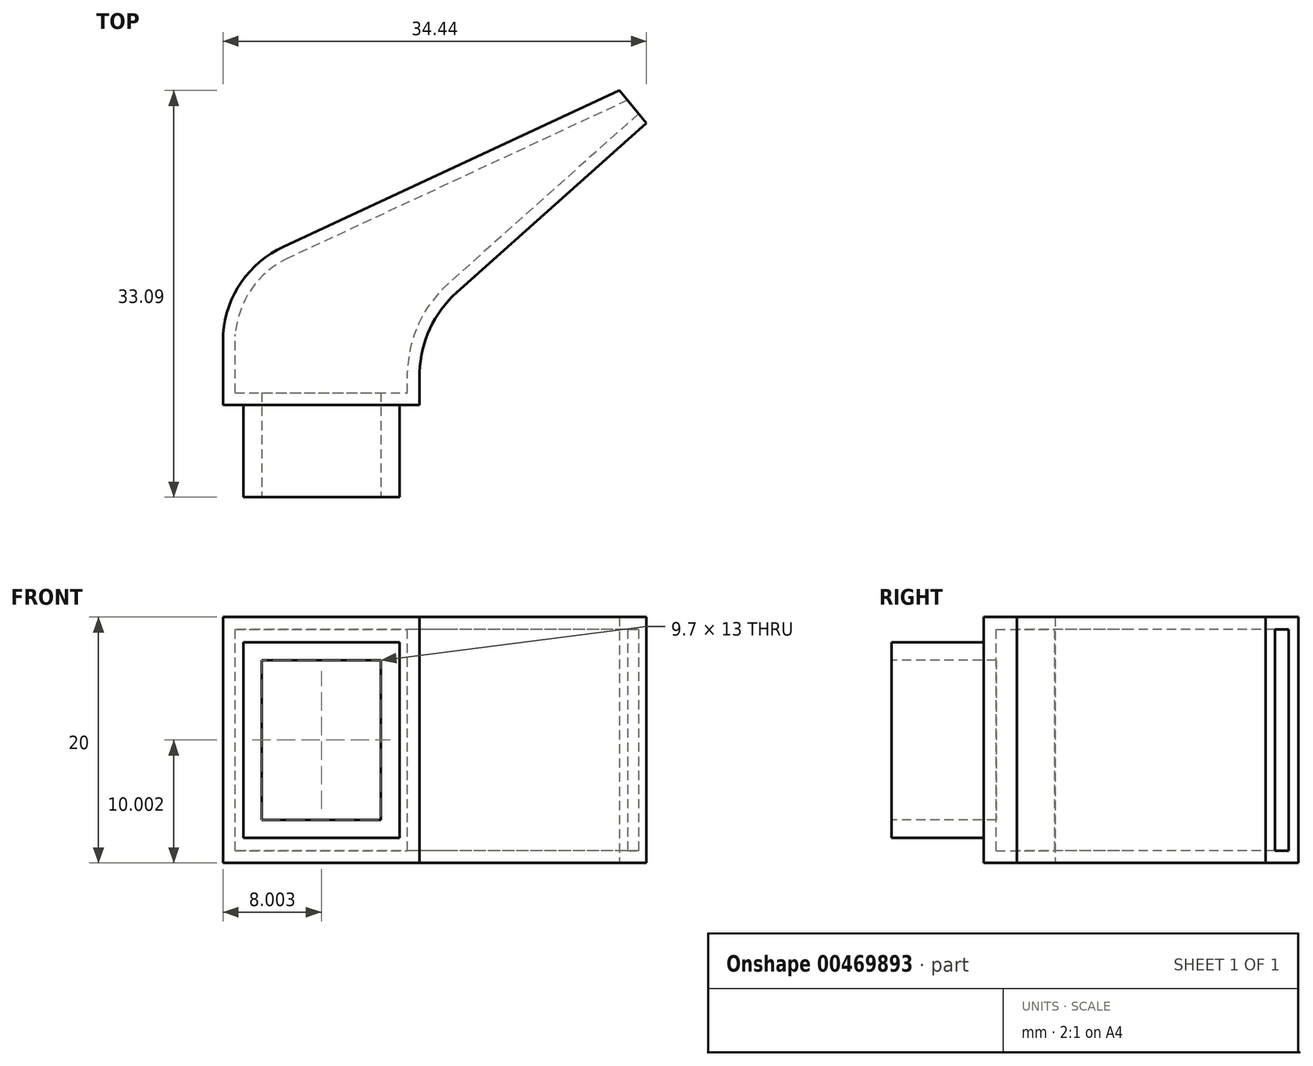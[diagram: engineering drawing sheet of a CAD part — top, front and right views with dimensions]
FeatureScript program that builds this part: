
annotation { "Feature Type Name" : "Feature", "Feature Type Description" : "" }
export const myFeature = defineFeature(function(context is Context, id is Id, definition is map)
    precondition{}
    {
        {
            var Q0;
            Q0=qCreatedBy(makeId("Front.planeOp"),FACE);
            var sketch = newSketch(context, id + "F0", { "sketchPlane" : qUnion([Q0])});
            skLineSegment(sketch, "E0.bottom", {"start": v(-17.22, 10) * mm, "end": v(17.22, 10) * mm});
            skLineSegment(sketch, "E0.top", {"start": v(-17.22, -10) * mm, "end": v(17.22, -10) * mm});
            skLineSegment(sketch, "E0.left", {"start": v(-17.22, 10) * mm, "end": v(-17.22, -10) * mm});
            skPoint(sketch, "E0.middle", {"position": v(0.21, 0.04) * mm});
            skPoint(sketch, "E1.middle", {"position": v(-0.07, 0.04) * mm});
            skLineSegment(sketch, "E2.bottom", {"start": v(-14.07, 6.5) * mm, "end": v(-4.37, 6.5) * mm});
            skLineSegment(sketch, "E2.top", {"start": v(-14.07, -6.5) * mm, "end": v(-4.37, -6.5) * mm});
            skLineSegment(sketch, "E2.left", {"start": v(-14.07, 6.5) * mm, "end": v(-14.07, -6.5) * mm});
            skLineSegment(sketch, "E2.right", {"start": v(-4.37, 6.5) * mm, "end": v(-4.37, -6.5) * mm});
            skLineSegment(sketch, "E3.bottom", {"start": v(-15.57, 7.96) * mm, "end": v(-2.87, 7.96) * mm});
            skLineSegment(sketch, "E3.top", {"start": v(-15.57, -7.96) * mm, "end": v(-2.87, -7.96) * mm});
            skLineSegment(sketch, "E3.left", {"start": v(-15.57, 7.96) * mm, "end": v(-15.57, -7.96) * mm});
            skLineSegment(sketch, "E3.right", {"start": v(-2.87, 7.96) * mm, "end": v(-2.87, -7.96) * mm});
            skLineSegment(sketch, "E4.0", {"start": v(17.22, 10) * mm, "end": v(17.22, -10) * mm});
            skLineSegment(sketch, "E5.0", {"start": v(-1.22, 10) * mm, "end": v(-1.22, -10) * mm});
            skSolve(sketch);
        }
        {
            var Q0;
            Q0=qCreatedBy(makeId("Top.planeOp"),FACE);
            var sketch = newSketch(context, id + "F1", { "sketchPlane" : qUnion([Q0])});
            skLineSegment(sketch, "E6.bottom", {"start": v(-15.57, -7.3) * mm, "end": v(-2.87, -7.3) * mm});
            skLineSegment(sketch, "E6.top", {"start": v(-15.57, 0) * mm, "end": v(-2.87, 0) * mm});
            skLineSegment(sketch, "E6.left", {"start": v(-15.57, -7.3) * mm, "end": v(-15.57, 0) * mm});
            skLineSegment(sketch, "E6.right", {"start": v(-2.87, -7.3) * mm, "end": v(-2.87, 0) * mm});
            skLineSegment(sketch, "E7", {"start": v(-15.57, 0) * mm, "end": v(-17.22, 0) * mm});
            skLineSegment(sketch, "E8", {"start": v(-2.87, 0) * mm, "end": v(-1.22, 0) * mm});
            skLineSegment(sketch, "E9", {"start": v(15.02, 25.59) * mm, "end": v(17.22, 22.91) * mm});
            skLineSegment(sketch, "E10", {"start": v(15.02, 25.59) * mm, "end": v(-12.3, 12.88) * mm});
            skArc(sketch, "E11", {"start": v(-12.3, 12.88) * mm, "mid": v(-15.72, 10) * mm, "end": v(-17.22, 5.79) * mm});
            skLineSegment(sketch, "E12", {"start": v(17.22, 22.91) * mm, "end": v(1.78, 9.14) * mm});
            skArc(sketch, "E13", {"start": v(1.78, 9.14) * mm, "mid": v(-0.38, 6.22) * mm, "end": v(-1.22, 2.68) * mm});
            skLineSegment(sketch, "E14", {"start": v(-17.22, 0) * mm, "end": v(-17.22, 5.79) * mm});
            skLineSegment(sketch, "E15", {"start": v(-1.22, 0) * mm, "end": v(-1.22, 2.68) * mm});
            skSolve(sketch);
        }
        {
            var Q0;
            Q0=makeQuery(id+"F1.imprint","IMPRINT",FACE,{"disambiguationData":[TD([[makeQuery(id+"F1.imprint","IMPRINT",EDGE,{"derivedFrom":sQuery(id+"F1.wireOp",EDGE,"E6.top")}),1.0]])]});
            extrude(context, id + "F2", {"entities" : qUnion([Q0]), "endBound" : BoundingType.SYMMETRIC, "depth" : 20 * mm});
        }
        {
            var Q0;
            Q0=makeQuery(id+"F2.opExtrude","SWEPT_FACE",FACE,{"disambiguationData":[OSD([sQuery(id+"F1.wireOp",EDGE,"E9")])]});
            var Q1;
            Q1=makeQuery(id+"F2.opExtrude","SWEPT_FACE",FACE,{"disambiguationData":[OSD([sQuery(id+"F1.wireOp",EDGE,"E6.top"),sQuery(id+"F1.wireOp",EDGE,"E7"),sQuery(id+"F1.wireOp",EDGE,"E8")])]});
            shell(context, id + "F3", {"entities" : qUnion([Q0, Q1]), "thickness" : 1 * mm});
        }
        {
            var Q0;
            {var subQ0=sQuery(id+"F0.wireOp",EDGE,"E0.left");Q0=makeQuery(id+"F0.imprint","IMPRINT",FACE,{"disambiguationData":[TD([[makeQuery(id+"F0.imprint","IMPRINT",EDGE,{"derivedFrom":subQ0}),1.0]])]});}
            var Q1;
            Q1=makeQuery(id+"F0.imprint","IMPRINT",FACE,{"disambiguationData":[TD([[makeQuery(id+"F0.imprint","IMPRINT",EDGE,{"derivedFrom":sQuery(id+"F0.wireOp",EDGE,"E2.bottom")}),1.0]])]});
            extrude(context, id + "F4", {"entities" : qUnion([Q0, Q1]), "operationType" : NewBodyOperationType.ADD, "oppositeDirection" : true, "depth" : 1 * mm});
        }
        {
            var Q0;
            Q0=makeQuery(id+"F0.imprint","IMPRINT",FACE,{"disambiguationData":[TD([[makeQuery(id+"F0.imprint","IMPRINT",EDGE,{"derivedFrom":sQuery(id+"F0.wireOp",EDGE,"E2.bottom")}),1.0]])]});
            extrude(context, id + "F5", {"entities" : qUnion([Q0]), "operationType" : NewBodyOperationType.ADD, "depth" : 7.5 * mm});
        }
    });
